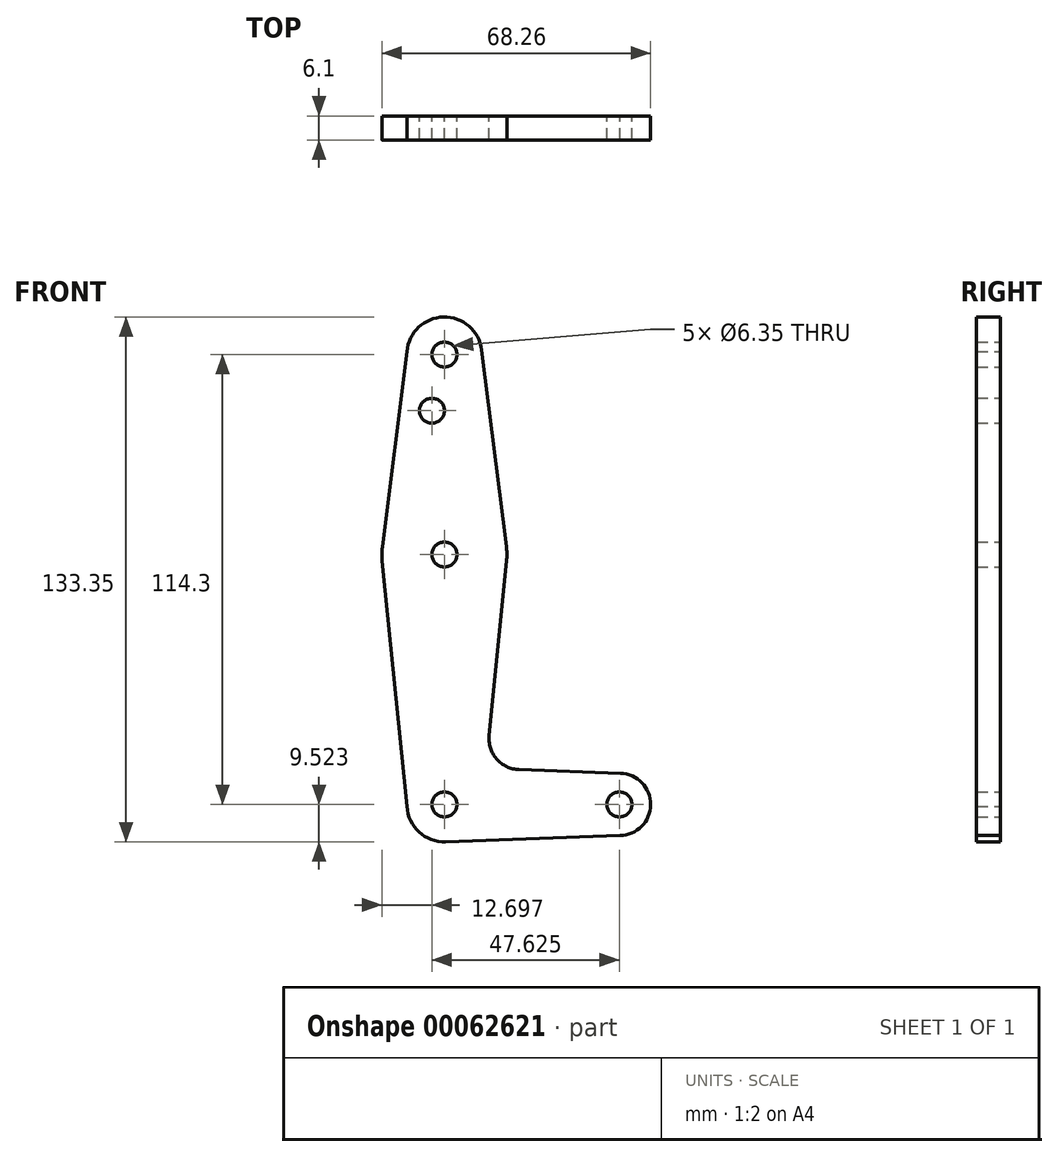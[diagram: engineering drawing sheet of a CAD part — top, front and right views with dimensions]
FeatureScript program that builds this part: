
annotation { "Feature Type Name" : "Feature", "Feature Type Description" : "" }
export const myFeature = defineFeature(function(context is Context, id is Id, definition is map)
    precondition{}
    {
        {
            var Q0;
            Q0=qCreatedBy(makeId("Front.planeOp"),FACE);
            var sketch = newSketch(context, id + "F0", { "sketchPlane" : qUnion([Q0])});
            skLineSegment(sketch, "E0", {"start": v(-57, 81.01) * mm, "end": v(-57, -33.29) * mm, "construction": true});
            skLineSegment(sketch, "E1", {"start": v(-57, -33.29) * mm, "end": v(-12.55, -33.29) * mm, "construction": true});
            skCircle(sketch, "E2", {"center": v(-57, 81.01) * mm, "radius": 9.53 * mm});
            skCircle(sketch, "E3", {"center": v(-57, 30.21) * mm, "radius": 15.88 * mm});
            skCircle(sketch, "E4", {"center": v(-57, -33.29) * mm, "radius": 9.53 * mm});
            skCircle(sketch, "E5", {"center": v(-12.55, -33.29) * mm, "radius": 7.94 * mm});
            skLineSegment(sketch, "E6", {"start": v(-47.55, 82.2) * mm, "end": v(-41.25, 32.2) * mm});
            skLineSegment(sketch, "E7", {"start": v(-41.2, 28.63) * mm, "end": v(-45.66, -15.7) * mm});
            skLineSegment(sketch, "E8", {"start": v(-66.5, -33.79) * mm, "end": v(-72.8, 28.62) * mm});
            skLineSegment(sketch, "E9", {"start": v(-38.03, -24.44) * mm, "end": v(-12.27, -25.35) * mm});
            skLineSegment(sketch, "E10", {"start": v(-12.4, -41.22) * mm, "end": v(-56.66, -42.8) * mm});
            skCircle(sketch, "E11", {"center": v(-57, 30.21) * mm, "radius": 3.18 * mm});
            skCircle(sketch, "E12", {"center": v(-57, 81.01) * mm, "radius": 3.18 * mm});
            skCircle(sketch, "E13", {"center": v(-57, -33.29) * mm, "radius": 3.18 * mm});
            skCircle(sketch, "E14", {"center": v(-12.55, -33.29) * mm, "radius": 3.18 * mm});
            skArc(sketch, "E15.filletArc", {"start": v(-45.66, -15.7) * mm, "mid": v(-43.74, -21.72) * mm, "end": v(-38.03, -24.44) * mm});
            skLineSegment(sketch, "E16", {"start": v(-66.5, 81.8) * mm, "end": v(-72.75, 32.2) * mm});
            skCircle(sketch, "E17", {"center": v(-60.17, 66.74) * mm, "radius": 3.18 * mm});
            skSolve(sketch);
        }
        {
            var Q0;
            Q0 = qSketchRegion(id + "F0", true);
            extrude(context, id + "F1", {"entities" : qUnion([Q0]), "depth" : 3.05 * mm, "hasSecondDirection" : true, "secondDirectionOppositeDirection" : true, "secondDirectionDepth" : 3.05 * mm});
        }
    });
